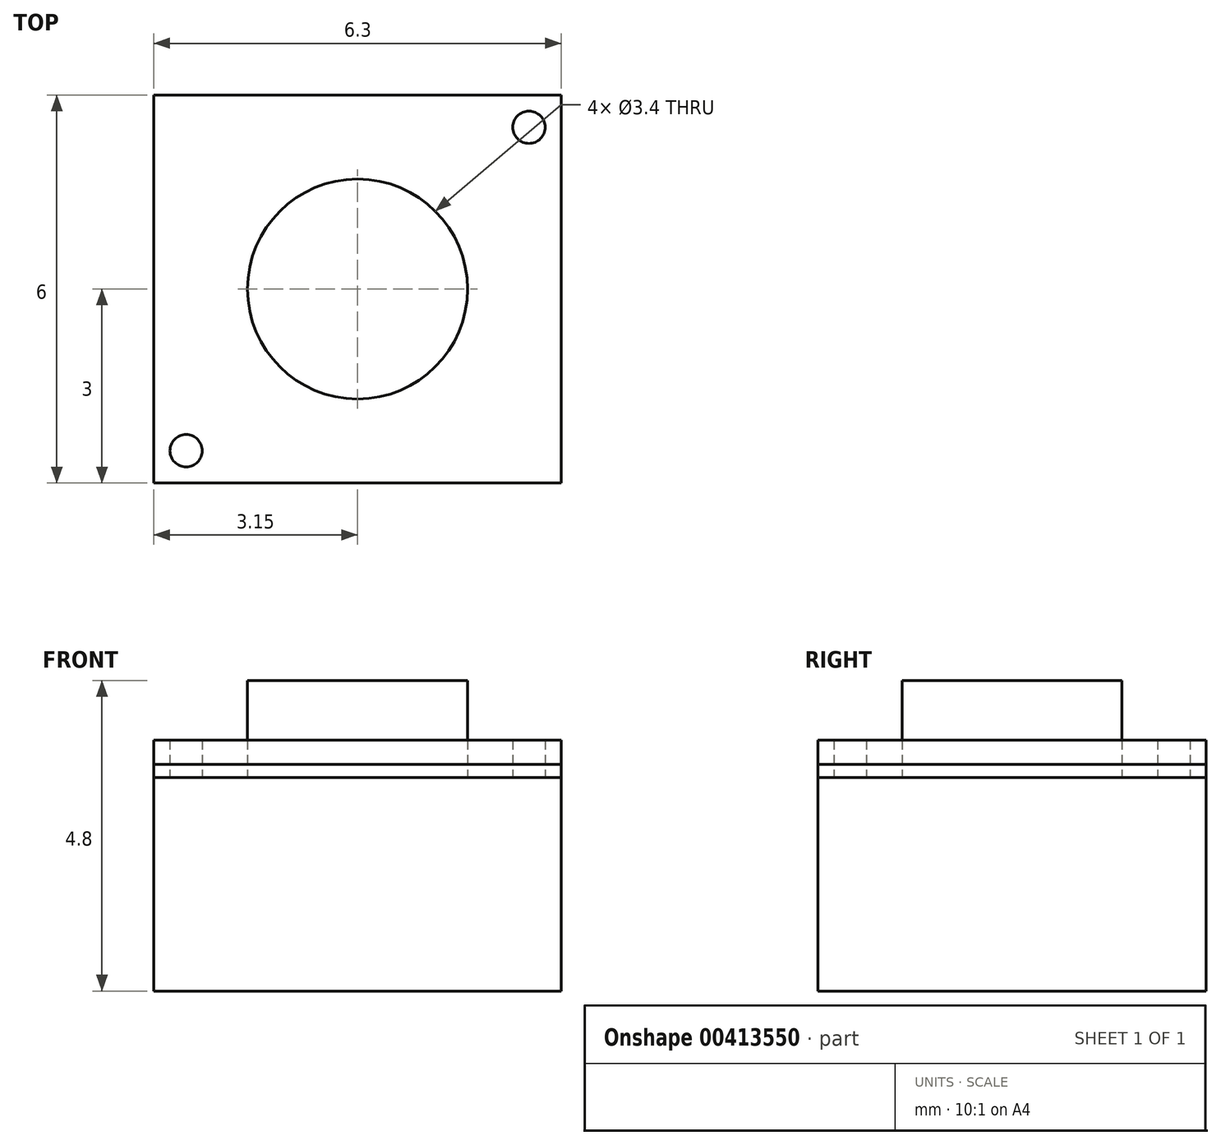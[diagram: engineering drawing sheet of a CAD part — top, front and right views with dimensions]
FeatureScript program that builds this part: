
annotation { "Feature Type Name" : "Feature", "Feature Type Description" : "" }
export const myFeature = defineFeature(function(context is Context, id is Id, definition is map)
    precondition{}
    {
        {
            var Q0;
            Q0=qCreatedBy(makeId("Top.planeOp"),FACE);
            var sketch = newSketch(context, id + "F0", { "sketchPlane" : qUnion([Q0])});
            skLineSegment(sketch, "E0.bottom", {"start": v(3.15, 3) * mm, "end": v(-3.15, 3) * mm});
            skLineSegment(sketch, "E0.top", {"start": v(3.15, -3) * mm, "end": v(-3.15, -3) * mm});
            skLineSegment(sketch, "E0.left", {"start": v(3.15, 3) * mm, "end": v(3.15, -3) * mm});
            skLineSegment(sketch, "E0.right", {"start": v(-3.15, 3) * mm, "end": v(-3.15, -3) * mm});
            skPoint(sketch, "E0.middle", {"position": v(0, 0) * mm});
            skSolve(sketch);
        }
        {
            var Q0;
            Q0 = qSketchRegion(id + "F0", true);
            extrude(context, id + "F1", {"entities" : qUnion([Q0]), "depth" : 3.3 * mm});
        }
        {
            var Q0;
            Q0=makeQuery(id+"F1.opExtrude","CAP_FACE",FACE,{"disambiguationData":[OSD([sQuery(id+"F0.wireOp",EDGE,"E0.bottom"),sQuery(id+"F0.wireOp",EDGE,"E0.top"),sQuery(id+"F0.wireOp",EDGE,"E0.left"),sQuery(id+"F0.wireOp",EDGE,"E0.right")])],"isStart":false});
            var sketch = newSketch(context, id + "F2", { "sketchPlane" : qUnion([Q0])});
            skLineSegment(sketch, "E1.bottom", {"start": v(-3.15, 3) * mm, "end": v(3.15, 3) * mm});
            skLineSegment(sketch, "E1.top", {"start": v(-3.15, -3) * mm, "end": v(3.15, -3) * mm});
            skLineSegment(sketch, "E1.left", {"start": v(-3.15, 3) * mm, "end": v(-3.15, -3) * mm});
            skLineSegment(sketch, "E1.right", {"start": v(3.15, 3) * mm, "end": v(3.15, -3) * mm});
            skSolve(sketch);
        }
        {
            var Q0;
            Q0 = qSketchRegion(id + "F2", true);
            extrude(context, id + "F3", {"entities" : qUnion([Q0]), "depth" : 0.2 * mm});
        }
        {
            var Q0;
            Q0=makeQuery(id+"F1.opExtrude","CAP_FACE",FACE,{"disambiguationData":[OSD([sQuery(id+"F0.wireOp",EDGE,"E0.bottom"),sQuery(id+"F0.wireOp",EDGE,"E0.top"),sQuery(id+"F0.wireOp",EDGE,"E0.left"),sQuery(id+"F0.wireOp",EDGE,"E0.right")])],"isStart":false});
            var sketch = newSketch(context, id + "F4", { "sketchPlane" : qUnion([Q0])});
            skCircle(sketch, "E2", {"center": v(0, 0) * mm, "radius": 1.7 * mm});
            skCircle(sketch, "E3", {"center": v(-2.65, 2.5) * mm, "radius": 0.25 * mm});
            skCircle(sketch, "E4.MirrorC", {"center": v(2.65, 2.5) * mm, "radius": 0.25 * mm});
            skCircle(sketch, "E5.MirrorC", {"center": v(2.65, -2.5) * mm, "radius": 0.25 * mm});
            skCircle(sketch, "E6.MirrorC", {"center": v(-2.65, -2.5) * mm, "radius": 0.25 * mm});
            skSolve(sketch);
        }
        {
            var Q0;
            Q0=makeQuery(id+"F4.imprint","IMPRINT",FACE,{"disambiguationData":[TD([[makeQuery(id+"F4.imprint","IMPRINT",EDGE,{"derivedFrom":sQuery(id+"F4.wireOp",EDGE,"E2")}),1.0]])]});
            extrude(context, id + "F5", {"entities" : qUnion([Q0]), "depth" : 1.5 * mm});
        }
        {
            var Q0;
            Q0=makeQuery(id+"F4.imprint","IMPRINT",FACE,{"disambiguationData":[TD([[makeQuery(id+"F4.imprint","IMPRINT",EDGE,{"derivedFrom":sQuery(id+"F4.wireOp",EDGE,"E3")}),1.0]])]});
            var Q1;
            Q1=makeQuery(id+"F4.imprint","IMPRINT",FACE,{"disambiguationData":[TD([[makeQuery(id+"F4.imprint","IMPRINT",EDGE,{"derivedFrom":sQuery(id+"F4.wireOp",EDGE,"E4.MirrorC")}),-1.0]])]});
            var Q2;
            Q2=makeQuery(id+"F4.imprint","IMPRINT",FACE,{"disambiguationData":[TD([[makeQuery(id+"F4.imprint","IMPRINT",EDGE,{"derivedFrom":sQuery(id+"F4.wireOp",EDGE,"E5.MirrorC")}),1.0]])]});
            var Q3;
            Q3=makeQuery(id+"F4.imprint","IMPRINT",FACE,{"disambiguationData":[TD([[makeQuery(id+"F4.imprint","IMPRINT",EDGE,{"derivedFrom":sQuery(id+"F4.wireOp",EDGE,"E6.MirrorC")}),-1.0]])]});
            extrude(context, id + "F6", {"entities" : qUnion([Q0, Q1, Q2, Q3]), "depth" : 0.58 * mm});
        }
    });
